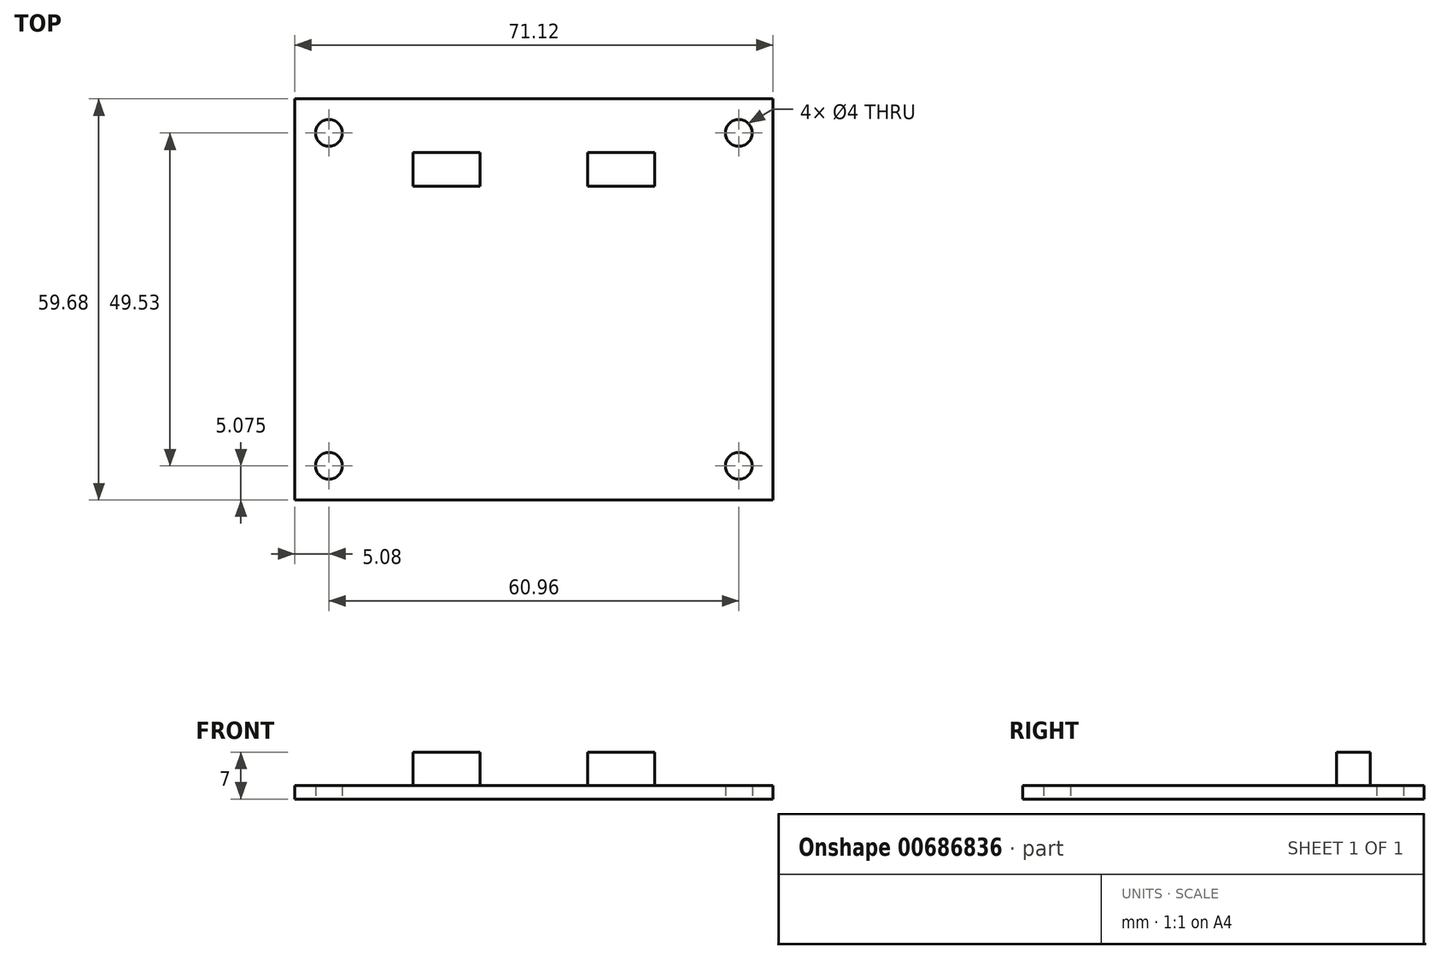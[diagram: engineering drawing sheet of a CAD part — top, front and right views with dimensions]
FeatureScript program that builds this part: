
annotation { "Feature Type Name" : "Feature", "Feature Type Description" : "" }
export const myFeature = defineFeature(function(context is Context, id is Id, definition is map)
    precondition{}
    {
        {
            var Q0;
            Q0=qCreatedBy(makeId("Top.planeOp"),FACE);
            var sketch = newSketch(context, id + "F0", { "sketchPlane" : qUnion([Q0])});
            skLineSegment(sketch, "E0.bottom", {"start": v(-35.56, 29.85) * mm, "end": v(35.56, 29.85) * mm});
            skLineSegment(sketch, "E0.top", {"start": v(-35.56, -29.85) * mm, "end": v(35.56, -29.85) * mm});
            skLineSegment(sketch, "E0.left", {"start": v(-35.56, 29.85) * mm, "end": v(-35.56, -29.84) * mm});
            skLineSegment(sketch, "E0.right", {"start": v(35.56, 29.85) * mm, "end": v(35.56, -29.85) * mm});
            skPoint(sketch, "E0.middle", {"position": v(0, 0) * mm});
            skCircle(sketch, "E1", {"center": v(-30.48, 24.77) * mm, "radius": 2 * mm});
            skCircle(sketch, "E2.MirrorC", {"center": v(30.48, 24.77) * mm, "radius": 2 * mm});
            skCircle(sketch, "E3.MirrorC", {"center": v(-30.48, -24.77) * mm, "radius": 2 * mm});
            skCircle(sketch, "E4.MirrorC", {"center": v(30.48, -24.76) * mm, "radius": 2 * mm});
            skSolve(sketch);
        }
        {
            var Q0;
            Q0 = qSketchRegion(id + "F0", true);
            extrude(context, id + "F1", {"entities" : qUnion([Q0]), "depth" : 2 * mm, "offsetDistance" : 25 * mm});
        }
        {
            var Q0;
            Q0=makeQuery(id+"F1.opExtrude","CAP_FACE",FACE,{"disambiguationData":[OSD([sQuery(id+"F0.wireOp",EDGE,"E0.bottom"),sQuery(id+"F0.wireOp",EDGE,"E0.top"),sQuery(id+"F0.wireOp",EDGE,"E0.left"),sQuery(id+"F0.wireOp",EDGE,"E0.right"),sQuery(id+"F0.wireOp",EDGE,"E1"),sQuery(id+"F0.wireOp",EDGE,"E2.MirrorC"),sQuery(id+"F0.wireOp",EDGE,"E3.MirrorC"),sQuery(id+"F0.wireOp",EDGE,"E4.MirrorC")])],"isStart":false});
            var sketch = newSketch(context, id + "F2", { "sketchPlane" : qUnion([Q0])});
            skLineSegment(sketch, "E5.bottom", {"start": v(-18, 16.85) * mm, "end": v(-8, 16.85) * mm});
            skLineSegment(sketch, "E5.top", {"start": v(-18, 21.85) * mm, "end": v(-8, 21.85) * mm});
            skLineSegment(sketch, "E5.left", {"start": v(-18, 16.85) * mm, "end": v(-18, 21.85) * mm});
            skLineSegment(sketch, "E5.right", {"start": v(-8, 16.85) * mm, "end": v(-8, 21.85) * mm});
            skLineSegment(sketch, "E6.MirrorCS", {"start": v(18, 16.85) * mm, "end": v(8, 16.85) * mm});
            skLineSegment(sketch, "E7.MirrorCS", {"start": v(18, 21.85) * mm, "end": v(8, 21.85) * mm});
            skLineSegment(sketch, "E8.MirrorCS", {"start": v(18, 16.85) * mm, "end": v(18, 21.85) * mm});
            skLineSegment(sketch, "E9.MirrorCS", {"start": v(8, 16.85) * mm, "end": v(8, 21.85) * mm});
            skSolve(sketch);
        }
        {
            var Q0;
            Q0 = qSketchRegion(id + "F2", true);
            extrude(context, id + "F3", {"entities" : qUnion([Q0]), "depth" : 5 * mm, "offsetDistance" : 25 * mm});
        }
    });
